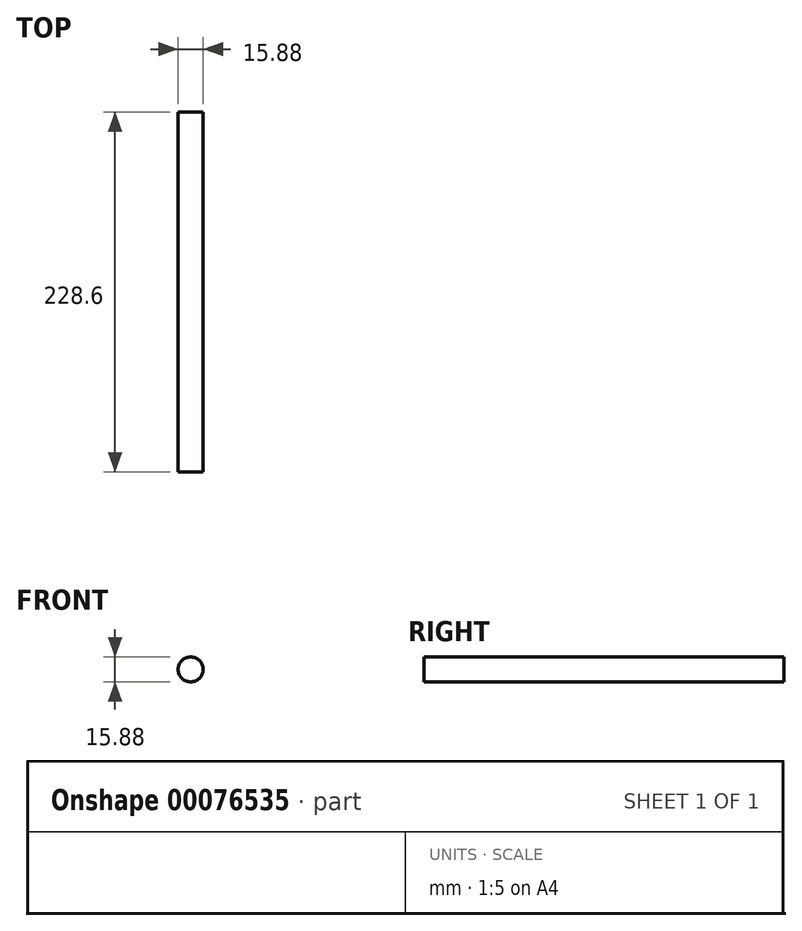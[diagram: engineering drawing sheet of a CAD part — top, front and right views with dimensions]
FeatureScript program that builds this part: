
annotation { "Feature Type Name" : "Feature", "Feature Type Description" : "" }
export const myFeature = defineFeature(function(context is Context, id is Id, definition is map)
    precondition{}
    {
        {
            var Q0;
            Q0=qCreatedBy(makeId("Front.planeOp"),FACE);
            var sketch = newSketch(context, id + "F0", { "sketchPlane" : qUnion([Q0])});
            skCircle(sketch, "E0", {"center": v(0, 0) * mm, "radius": 7.94 * mm});
            skSolve(sketch);
        }
        {
            var Q0;
            Q0=qSketchRegion(id+"F0",true);
            extrude(context, id + "F1", {"entities" : qUnion([Q0]), "depth" : 228.6 * mm});
        }
    });
